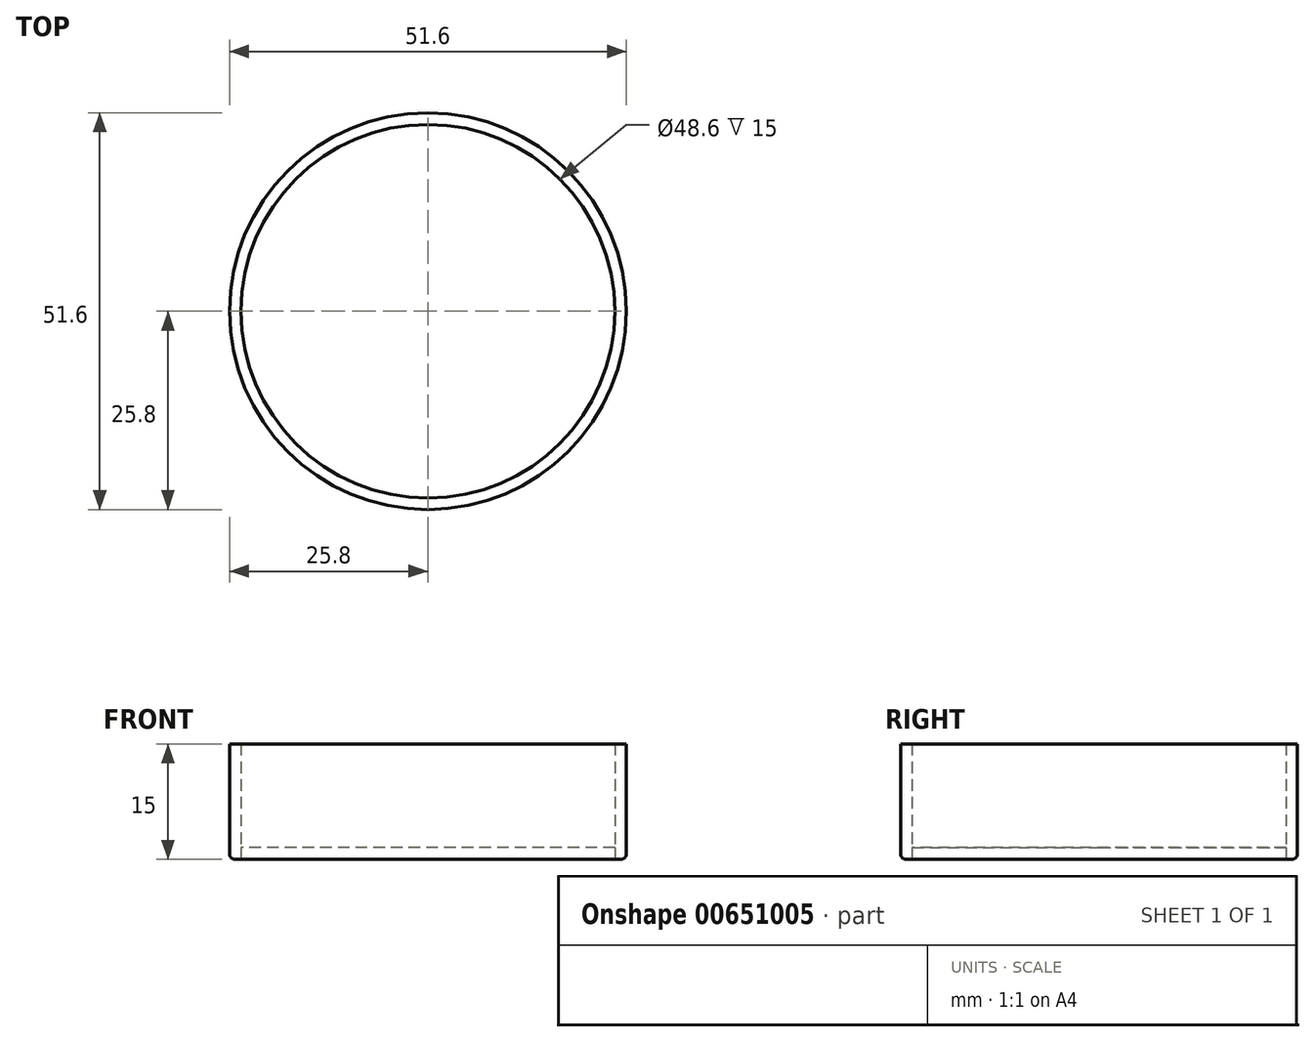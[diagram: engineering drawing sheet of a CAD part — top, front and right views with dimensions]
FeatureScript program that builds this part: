
annotation { "Feature Type Name" : "Feature", "Feature Type Description" : "" }
export const myFeature = defineFeature(function(context is Context, id is Id, definition is map)
    precondition{}
    {
        {
            var Q0;
            Q0=qCreatedBy(makeId("Top.planeOp"),FACE);
            var sketch = newSketch(context, id + "F0", { "sketchPlane" : qUnion([Q0])});
            skCircle(sketch, "E0", {"center": v(0, 0) * mm, "radius": 24.3 * mm});
            skCircle(sketch, "E1", {"center": v(0, 0) * mm, "radius": 25.8 * mm});
            skSolve(sketch);
        }
        {
            var Q0;
            Q0=makeQuery(id+"F0.imprint","IMPRINT",FACE,{"disambiguationData":[TD([[makeQuery(id+"F0.imprint","IMPRINT",EDGE,{"derivedFrom":sQuery(id+"F0.wireOp",EDGE,"E0")}),1.0]])]});
            extrude(context, id + "F1", {"entities" : qUnion([Q0]), "depth" : 1.5 * mm, "offsetDistance" : 25 * mm});
        }
        {
            var Q0;
            Q0=makeQuery(id+"F0.imprint","IMPRINT",FACE,{"disambiguationData":[TD([[makeQuery(id+"F0.imprint","IMPRINT",EDGE,{"derivedFrom":sQuery(id+"F0.wireOp",EDGE,"E0")}),-1.0]])]});
            extrude(context, id + "F2", {"entities" : qUnion([Q0]), "depth" : 15 * mm, "offsetDistance" : 25 * mm});
        }
        {
            var Q0;
            Q0=makeQuery(id+"F2.opExtrude","CAP_EDGE",EDGE,{"disambiguationData":[OSD([sQuery(id+"F0.wireOp",EDGE,"E1")])],"isStart":true});
            fillet(context, id + "F3", {"entities" : qUnion([Q0]), "radius" : 0.7 * mm, "tangentPropagation" : true, "allowEdgeOverflow" : false});
        }
    });
